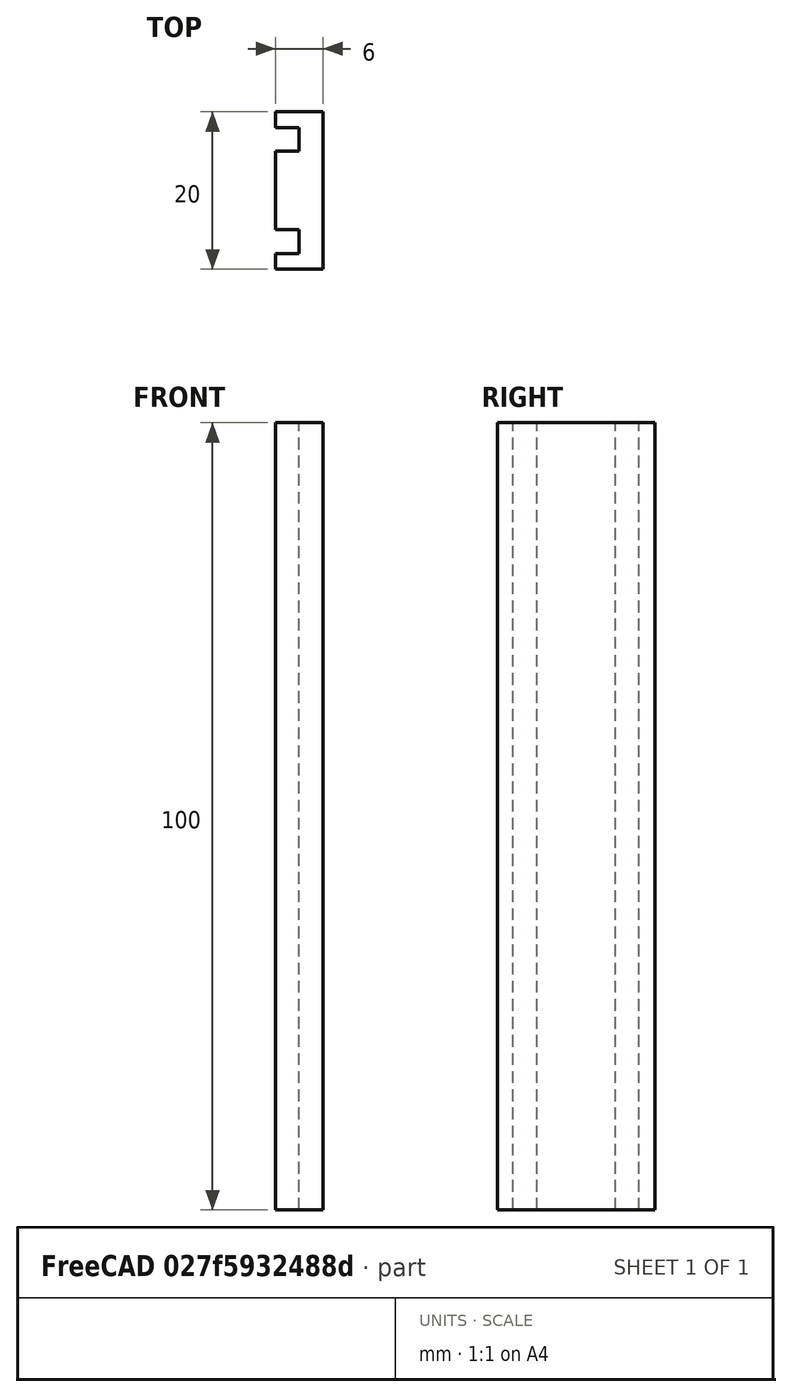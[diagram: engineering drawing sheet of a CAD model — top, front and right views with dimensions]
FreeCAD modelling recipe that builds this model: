
FCSTD DOCUMENT  (FreeCAD 1.0R39109 (Git))
Label: Rail
License: All rights reserved
LicenseURL: https://en.wikipedia.org/wiki/All_rights_reserved
objects: Spreadsheet::Sheet×1, Sketcher::SketchObject×1, Part::Extrusion×1
note: 3 computed .brp shape members not serialized (recipe doc carries the construction recipe); baked Part::Feature solids carry a one-line shape summary decoded from their .brp

FEATURE [Spreadsheet::Sheet] Spreadsheet
  cells = A1(railinPituus)=100; A2(SisaKorkeus)=10; A3(levynPaksuus)=3; A4(paksuus)=2; A5(insetti)=3
FEATURE [Sketcher::SketchObject] Sketch
  ArcFitTolerance = 1e-06
  FullyConstrained = true
  MakeInternals = false
  expr: Constraints[14] = Spreadsheet.paksuus
  expr: Constraints[17] = Spreadsheet.levynPaksuus + Spreadsheet.insetti
  expr: Constraints[20] = Spreadsheet.SisaKorkeus + 2 * Spreadsheet.levynPaksuus + 2 * Spreadsheet.paksuus
  expr: Constraints[2] = <<Spreadsheet>>.SisaKorkeus
  expr: Constraints[5] = <<Spreadsheet>>.insetti
  expr: Constraints[8] = <<Spreadsheet>>.levynPaksuus
  sketch-geometry (12):
    g0: LineSegment StartX=0 StartY=0 StartZ=0 EndX=0 EndY=10 EndZ=0
    g1: LineSegment StartX=0 StartY=10 StartZ=0 EndX=3 EndY=10 EndZ=0
    g2: LineSegment StartX=3 StartY=10 StartZ=0 EndX=3 EndY=13 EndZ=0
    g3: LineSegment StartX=3 StartY=13 StartZ=0 EndX=0 EndY=13 EndZ=0
    g4: LineSegment StartX=0 StartY=13 StartZ=0 EndX=0 EndY=15 EndZ=0
    g5: LineSegment StartX=0 StartY=15 StartZ=0 EndX=6 EndY=15 EndZ=0
    g6: LineSegment StartX=6 StartY=15 StartZ=0 EndX=6 EndY=-5 EndZ=0
    g7: LineSegment StartX=6 StartY=-5 StartZ=0 EndX=0 EndY=-5 EndZ=0
    g8: LineSegment StartX=0 StartY=-5 StartZ=0 EndX=0 EndY=-3 EndZ=0
    g9: LineSegment StartX=0 StartY=-3 StartZ=0 EndX=3 EndY=-3 EndZ=0
    g10: LineSegment StartX=3 StartY=-3 StartZ=0 EndX=3 EndY=0 EndZ=0
    g11: LineSegment StartX=3 StartY=0 StartZ=0 EndX=0 EndY=0 EndZ=0
  constraints (35):
    c: Coincident(g0,g-1)
    c: PointOnObject(g0,g-2)
    c: DistanceY(g0,g0) = 10
    c: Coincident(g1,g0)
    c: Horizontal(g1)
    c: DistanceX(g-1,g1) = 3
    c: Vertical(g2)
    c: Coincident(g2,g1)
    c: Distance(g2) = 3
    c: Coincident(g3,g2)
    c: PointOnObject(g3,g-2)
    c: Horizontal(g3)
    c: Coincident(g4,g3)
    c: PointOnObject(g4,g-2)
    c: Distance(g4) = 2
    c: Horizontal(g5)
    c: Coincident(g5,g4)
    c: Distance(g5) = 6
    c: Vertical(g6)
    c: Coincident(g6,g5)
    c: Distance(g6) = 20
    c: Coincident(g7,g6)
    c: PointOnObject(g7,g-2)
    c: Horizontal(g7)
    c: Distance(g8) = 2
    c: Coincident(g8,g7)
    c: PointOnObject(g8,g-2)
    c: Distance(g9) = 3
    c: Coincident(g9,g8)
    c: Horizontal(g9)
    c: Coincident(g10,g9)
    c: PointOnObject(g10,g-1)
    c: Vertical(g10)
    c: Coincident(g11,g10)
    c: Coincident(g11,g-1)
FEATURE [Part::Extrusion] Extrude
  Base = -> Sketch
  Dir = (0,0,1)
  DirMode = 2
  FaceMakerClass = Part::FaceMakerBullseye
  FaceMakerMode = 3
  LengthFwd = 100
  LengthRev = 0
  Solid = true
  Symmetric = false
  expr: LengthFwd = Spreadsheet.railinPituus
